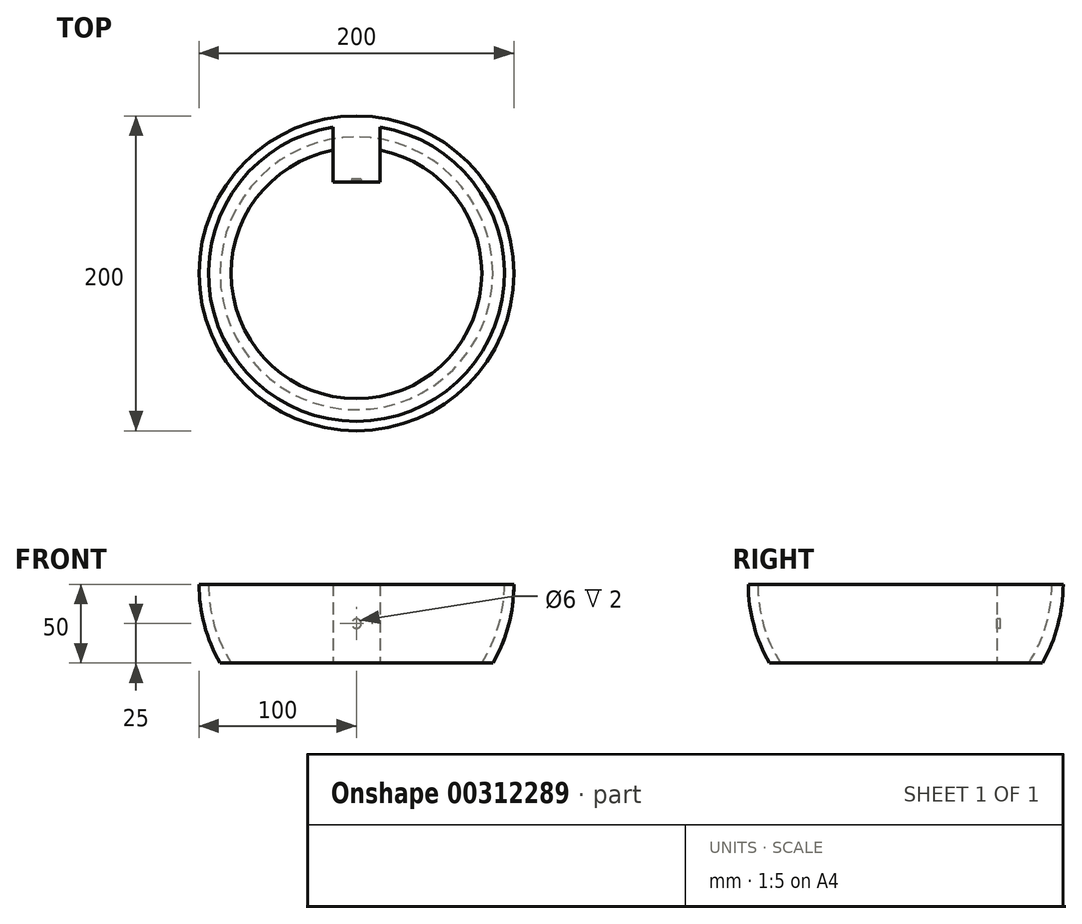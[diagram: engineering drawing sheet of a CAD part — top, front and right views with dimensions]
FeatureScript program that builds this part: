
annotation { "Feature Type Name" : "Feature", "Feature Type Description" : "" }
export const myFeature = defineFeature(function(context is Context, id is Id, definition is map)
    precondition{}
    {
        {
            var Q0;
            Q0=qCreatedBy(makeId("Front.planeOp"),FACE);
            var sketch = newSketch(context, id + "F0", { "sketchPlane" : qUnion([Q0])});
            skArc(sketch, "E0", {"start": v(-100, 0) * mm, "mid": v(-96.6, -25.88) * mm, "end": v(-86.6, -50) * mm});
            skLineSegment(sketch, "E1", {"start": v(0, 0) * mm, "end": v(0, -50) * mm});
            skLineSegment(sketch, "E2", {"start": v(0, -50) * mm, "end": v(-86.6, -50) * mm});
            skLineSegment(sketch, "E3", {"start": v(0, 0) * mm, "end": v(-100, 0) * mm});
            skPoint(sketch, "E4.orphan", {"position": v(0, 100) * mm});
            skSolve(sketch);
        }
        {
            var Q0;
            Q0=qSketchRegion(id+"F0",true);
            var Q1;
            Q1=sQuery(id+"F0.wireOp",EDGE,"E1");
            revolve(context, id + "F1", {"entities" : qUnion([Q0]), "axis" : qUnion([Q1]), "revolveType" : RevolveType.FULL});
        }
        {
            var Q0;
            Q0=makeQuery(id+"F1.opRevolve","SWEPT_FACE",FACE,{"disambiguationData":[OSD([sQuery(id+"F0.wireOp",EDGE,"E3")])]});
            var Q1;
            Q1=makeQuery(id+"F1.opRevolve","SWEPT_FACE",FACE,{"disambiguationData":[OSD([sQuery(id+"F0.wireOp",EDGE,"E2")])]});
            shell(context, id + "F2", {"entities" : qUnion([Q0, Q1]), "thickness" : 6 * mm});
        }
        {
            var Q0;
            Q0=qCreatedBy(makeId("Front.planeOp"),FACE);
            cPlane(context, id + "F3", {"entities" : qUnion([Q0]), "cplaneType" : CPlaneType.OFFSET, "offset" : 58 * mm, "oppositeDirection" : true, "width" : 150 * mm, "height" : 150 * mm});
        }
        {
            var Q0;
            Q0=qCreatedBy(id+"F3.planeOp",FACE);
            var sketch = newSketch(context, id + "F4", { "sketchPlane" : qUnion([Q0])});
            skLineSegment(sketch, "E5.0", {"start": v(-15, 0) * mm, "end": v(15, 0) * mm});
            skLineSegment(sketch, "E6.0", {"start": v(-15, -50) * mm, "end": v(15, -50) * mm});
            skLineSegment(sketch, "E7", {"start": v(15, 0) * mm, "end": v(15, -50) * mm});
            skLineSegment(sketch, "E8", {"start": v(15, -50) * mm, "end": v(12.48, -48.82) * mm});
            skLineSegment(sketch, "E9", {"start": v(-15, 0) * mm, "end": v(-15, -50) * mm});
            skPoint(sketch, "E10.orphan", {"position": v(-86.6, -50) * mm});
            skPoint(sketch, "E11.orphan", {"position": v(-100, 0) * mm});
            skPoint(sketch, "E12.orphan", {"position": v(100, 0) * mm});
            skPoint(sketch, "E13.orphan", {"position": v(86.6, -50) * mm});
            skSolve(sketch);
        }
        {
            var Q0;
            Q0=qSketchRegion(id+"F4",true);
            extrude(context, id + "F5", {"entities" : qUnion([Q0]), "operationType" : NewBodyOperationType.ADD, "endBound" : BoundingType.UP_TO_NEXT, "oppositeDirection" : true, "depth" : 25 * mm});
        }
        {
            var Q0;
            Q0=makeQuery(id+"F5.opExtrude","CAP_FACE",FACE,{"disambiguationData":[OSD([sQuery(id+"F4.wireOp",EDGE,"E5.0"),sQuery(id+"F4.wireOp",EDGE,"E6.0"),sQuery(id+"F4.wireOp",EDGE,"E7"),sQuery(id+"F4.wireOp",EDGE,"E9")])],"isStart":true});
            var sketch = newSketch(context, id + "F6", { "sketchPlane" : qUnion([Q0])});
            skCircle(sketch, "E14", {"center": v(0, -25) * mm, "radius": 3 * mm});
            skSolve(sketch);
        }
        {
            var Q0;
            Q0=qSketchRegion(id+"F6",true);
            extrude(context, id + "F7", {"entities" : qUnion([Q0]), "operationType" : NewBodyOperationType.REMOVE, "oppositeDirection" : true, "depth" : 2 * mm});
        }
    });
